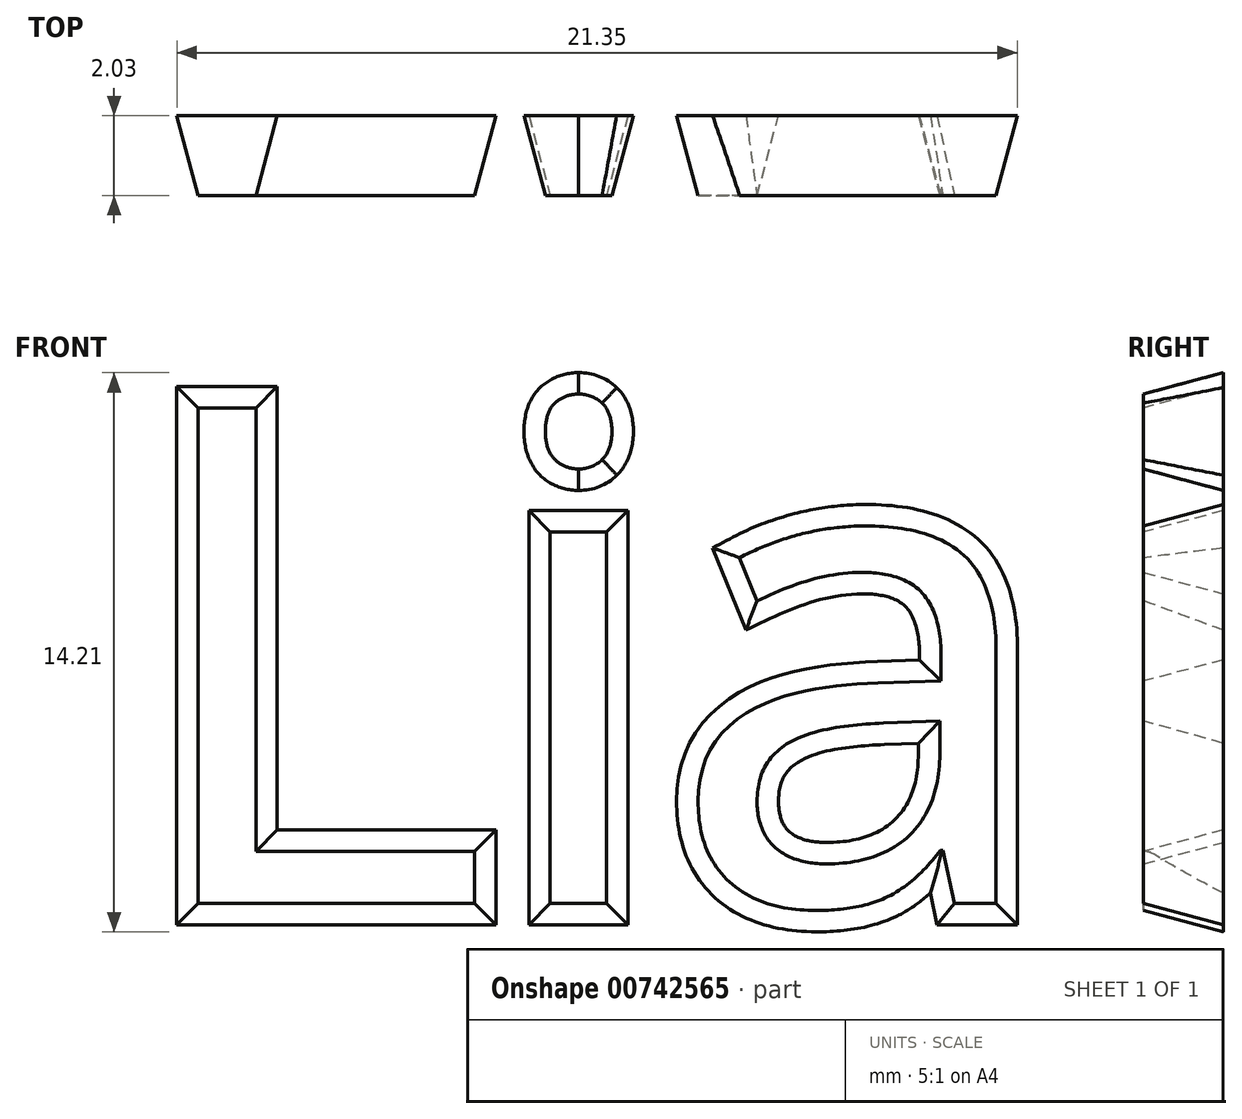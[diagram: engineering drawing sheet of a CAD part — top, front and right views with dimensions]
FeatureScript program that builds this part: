
annotation { "Feature Type Name" : "Feature", "Feature Type Description" : "" }
export const myFeature = defineFeature(function(context is Context, id is Id, definition is map)
    precondition{}
    {
        {
            var Q0;
            Q0=qCreatedBy(makeId("Front.planeOp"),FACE);
            var sketch = newSketch(context, id + "F0", { "sketchPlane" : qUnion([Q0])});
            skLineSegment(sketch, "E0.bottom", {"start": v(-25.4, 15.88) * mm, "end": v(25.4, 15.88) * mm});
            skLineSegment(sketch, "E0.top", {"start": v(-25.4, -15.88) * mm, "end": v(25.4, -15.88) * mm});
            skLineSegment(sketch, "E0.left", {"start": v(-25.4, 15.88) * mm, "end": v(-25.4, -15.88) * mm});
            skLineSegment(sketch, "E0.right", {"start": v(25.4, 15.87) * mm, "end": v(25.4, -15.88) * mm});
            skPoint(sketch, "E0.middle", {"position": v(0, 0) * mm});
            skSolve(sketch);
        }
        {
            var Q0;
            Q0=qCreatedBy(makeId("Front.planeOp"),FACE);
            var sketch = newSketch(context, id + "F1", { "sketchPlane" : qUnion([Q0])});
            skText(sketch, "E1", { "text": "Lia\n", "fontName": "OpenSans-Regular.ttf"});
            const initialGuessF1  = {"E1": [-0.01157, -0.00635, 1, 0, 0.0127]};
            skSetInitialGuess(sketch, initialGuessF1);
            skSolve(sketch);
        }
        {
            var Q0;
            Q0=qSketchRegion(id+"F1",true);
            extrude(context, id + "F2", {"entities" : qUnion([Q0]), "oppositeDirection" : true, "depth" : 2.03 * mm, "offsetDistance" : 25.4 * mm, "hasDraft" : true, "draftAngle" : 15 * degree});
        }
    });
